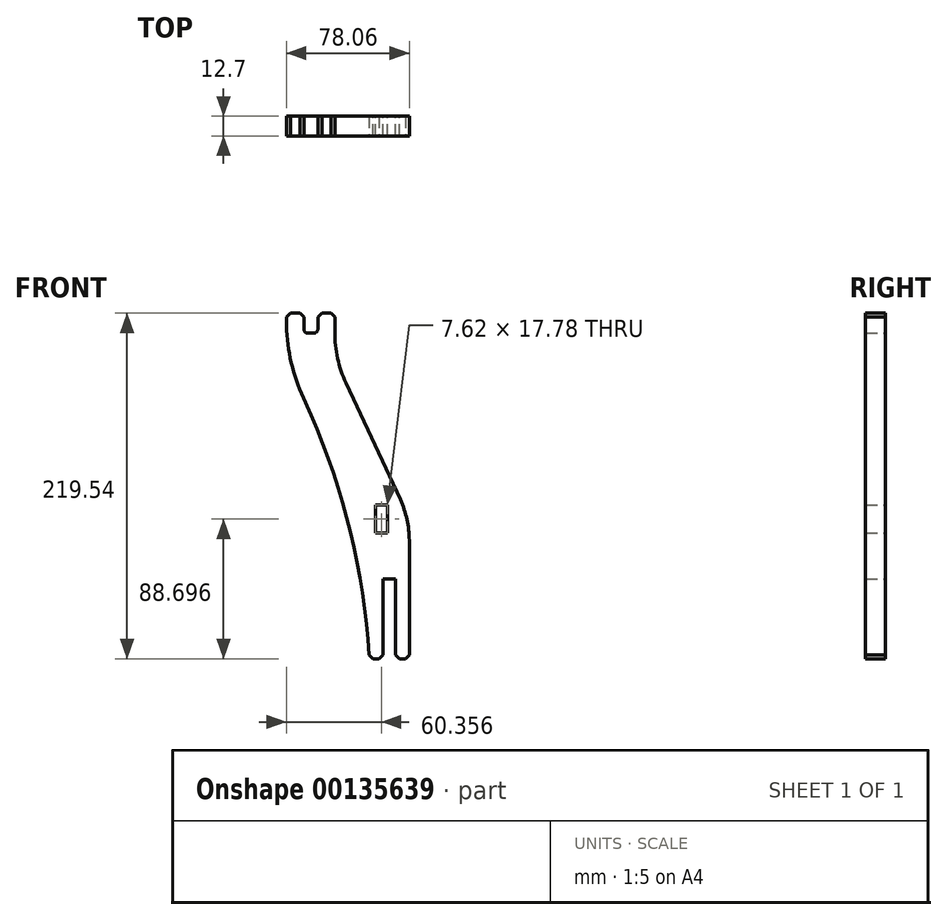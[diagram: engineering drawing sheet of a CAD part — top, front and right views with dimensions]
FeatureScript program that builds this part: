
annotation { "Feature Type Name" : "Feature", "Feature Type Description" : "" }
export const myFeature = defineFeature(function(context is Context, id is Id, definition is map)
    precondition{}
    {
        {
            var Q0;
            Q0=qCreatedBy(makeId("Front.planeOp"),FACE);
            var sketch = newSketch(context, id + "F0", { "sketchPlane" : qUnion([Q0])});
            skLineSegment(sketch, "E0.bottom", {"start": v(9.01, 35.53) * mm, "end": v(34.67, 35.53) * mm});
            skLineSegment(sketch, "E0.top", {"start": v(9.01, -35.53) * mm, "end": v(34.67, -35.53) * mm});
            skLineSegment(sketch, "E0.left", {"start": v(9.01, 35.53) * mm, "end": v(9.01, -35.53) * mm});
            skLineSegment(sketch, "E0.right", {"start": v(34.67, 35.53) * mm, "end": v(34.67, -35.53) * mm});
            skPoint(sketch, "E0.middle", {"position": v(21.84, 0) * mm});
            skLineSegment(sketch, "E1.bottom", {"start": v(17.9, -35.53) * mm, "end": v(25.78, -35.53) * mm});
            skLineSegment(sketch, "E1.top", {"start": v(17.9, 15.27) * mm, "end": v(25.78, 15.27) * mm});
            skLineSegment(sketch, "E1.left", {"start": v(17.9, -35.53) * mm, "end": v(17.9, 15.27) * mm});
            skLineSegment(sketch, "E1.right", {"start": v(25.78, -35.53) * mm, "end": v(25.78, 15.27) * mm});
            skLineSegment(sketch, "E2", {"start": v(34.67, 35.53) * mm, "end": v(34.67, 53.31) * mm});
            skLineSegment(sketch, "E3.bottom", {"start": v(-12.63, 154.91) * mm, "end": v(-43.39, 154.91) * mm});
            skLineSegment(sketch, "E3.top", {"start": v(-12.63, 184.01) * mm, "end": v(-43.39, 184.01) * mm});
            skLineSegment(sketch, "E3.left", {"start": v(-12.63, 154.91) * mm, "end": v(-12.63, 184.01) * mm});
            skLineSegment(sketch, "E3.right", {"start": v(-43.39, 154.91) * mm, "end": v(-43.39, 184.01) * mm});
            skPoint(sketch, "E3.middle", {"position": v(-28, 169.46) * mm});
            skLineSegment(sketch, "E4.bottom", {"start": v(-32.33, 184.01) * mm, "end": v(-23.44, 184.01) * mm});
            skLineSegment(sketch, "E4.top", {"start": v(-29.79, 171.31) * mm, "end": v(-25.98, 171.31) * mm});
            skLineSegment(sketch, "E4.left", {"start": v(-32.33, 184.01) * mm, "end": v(-32.33, 173.85) * mm});
            skLineSegment(sketch, "E4.right", {"start": v(-23.44, 184.01) * mm, "end": v(-23.44, 173.85) * mm});
            skLineSegment(sketch, "E5", {"start": v(-12.63, 154.91) * mm, "end": v(34.67, 53.31) * mm});
            skLineSegment(sketch, "E6", {"start": v(-43.39, 154.91) * mm, "end": v(9.01, 35.53) * mm});
            skPoint(sketch, "E7.visualSharp", {"position": v(-32.33, 171.31) * mm});
            skArc(sketch, "E7.filletArc", {"start": v(-32.33, 173.85) * mm, "mid": v(-31.58, 172.06) * mm, "end": v(-29.79, 171.31) * mm});
            skPoint(sketch, "E8.visualSharp", {"position": v(-23.44, 171.31) * mm});
            skArc(sketch, "E8.filletArc", {"start": v(-25.98, 171.31) * mm, "mid": v(-24.18, 172.06) * mm, "end": v(-23.44, 173.85) * mm});
            skLineSegment(sketch, "E9.bottom", {"start": v(13.16, 62.06) * mm, "end": v(20.78, 62.06) * mm});
            skLineSegment(sketch, "E9.top", {"start": v(13.16, 44.28) * mm, "end": v(20.78, 44.28) * mm});
            skLineSegment(sketch, "E9.left", {"start": v(13.16, 62.06) * mm, "end": v(13.16, 44.28) * mm});
            skLineSegment(sketch, "E9.right", {"start": v(20.78, 62.06) * mm, "end": v(20.78, 44.28) * mm});
            skSolve(sketch);
        }
        {
            var Q0;
            Q0=makeQuery(id+"F0.imprint","IMPRINT",FACE,{"disambiguationData":[TD([[makeQuery(id+"F0.imprint","IMPRINT",EDGE,{"derivedFrom":sQuery(id+"F0.wireOp",EDGE,"E3.bottom")}),-1.0]])]});
            var Q1;
            Q1=makeQuery(id+"F0.imprint","IMPRINT",FACE,{"disambiguationData":[TD([[makeQuery(id+"F0.imprint","IMPRINT",EDGE,{"derivedFrom":sQuery(id+"F0.wireOp",EDGE,"E0.bottom")}),1.0]])]});
            var Q2;
            Q2=makeQuery(id+"F0.imprint","IMPRINT",FACE,{"disambiguationData":[TD([[makeQuery(id+"F0.imprint","IMPRINT",EDGE,{"derivedFrom":sQuery(id+"F0.wireOp",EDGE,"E0.bottom")}),-1.0]])]});
            extrude(context, id + "F1", {"entities" : qUnion([Q0, Q1, Q2]), "depth" : 12.7 * mm});
        }
        {
            var Q0;
            Q0=makeQuery(id+"F1.opExtrude","SWEPT_EDGE",EDGE,{"disambiguationData":[OSD([sQuery(id+"F0.wireOp",EDGE,"E3.top"),sQuery(id+"F0.wireOp",EDGE,"E4.bottom"),sQuery(id+"F0.wireOp",EDGE,"E4.left")])]});
            var Q1;
            Q1=makeQuery(id+"F1.opExtrude","SWEPT_EDGE",EDGE,{"disambiguationData":[OSD([sQuery(id+"F0.wireOp",EDGE,"E3.top"),sQuery(id+"F0.wireOp",EDGE,"E4.bottom"),sQuery(id+"F0.wireOp",EDGE,"E4.right")])]});
            var Q2;
            Q2=makeQuery(id+"F1.opExtrude","SWEPT_EDGE",EDGE,{"disambiguationData":[OSD([sQuery(id+"F0.wireOp",EDGE,"E3.top"),sQuery(id+"F0.wireOp",EDGE,"E3.left")])]});
            var Q3;
            Q3=makeQuery(id+"F1.opExtrude","SWEPT_EDGE",EDGE,{"disambiguationData":[OSD([sQuery(id+"F0.wireOp",EDGE,"E3.top"),sQuery(id+"F0.wireOp",EDGE,"E3.right")])]});
            var Q4;
            Q4=makeQuery(id+"F1.opExtrude","SWEPT_EDGE",EDGE,{"disambiguationData":[OSD([sQuery(id+"F0.wireOp",EDGE,"E0.top"),sQuery(id+"F0.wireOp",EDGE,"E1.bottom"),sQuery(id+"F0.wireOp",EDGE,"E1.left")])]});
            var Q5;
            Q5=makeQuery(id+"F1.opExtrude","SWEPT_EDGE",EDGE,{"disambiguationData":[OSD([sQuery(id+"F0.wireOp",EDGE,"E0.top"),sQuery(id+"F0.wireOp",EDGE,"E1.bottom"),sQuery(id+"F0.wireOp",EDGE,"E1.right")])]});
            var Q6;
            Q6=makeQuery(id+"F1.opExtrude","SWEPT_EDGE",EDGE,{"disambiguationData":[OSD([sQuery(id+"F0.wireOp",EDGE,"E0.top"),sQuery(id+"F0.wireOp",EDGE,"E0.right")])]});
            var Q7;
            Q7=makeQuery(id+"F1.opExtrude","SWEPT_EDGE",EDGE,{"disambiguationData":[OSD([sQuery(id+"F0.wireOp",EDGE,"E0.top"),sQuery(id+"F0.wireOp",EDGE,"E0.left")])]});
            chamfer(context, id + "F2", {"entities" : qUnion([Q0, Q1, Q2, Q3, Q4, Q5, Q6, Q7]), "width" : 2.54 * mm, "tangentPropagation" : true});
        }
        {
            var Q0;
            Q0=makeQuery(id+"F1.opExtrude","SWEPT_EDGE",EDGE,{"disambiguationData":[OSD([sQuery(id+"F0.wireOp",EDGE,"E2"),sQuery(id+"F0.wireOp",EDGE,"E5")])]});
            fillet(context, id + "F3", {"entities" : qUnion([Q0]), "radius" : 61.32 * mm, "tangentPropagation" : true, "allowEdgeOverflow" : false});
        }
        {
            var Q0;
            Q0=makeQuery(id+"F1.opExtrude","SWEPT_EDGE",EDGE,{"disambiguationData":[OSD([sQuery(id+"F0.wireOp",EDGE,"E3.bottom"),sQuery(id+"F0.wireOp",EDGE,"E3.left"),sQuery(id+"F0.wireOp",EDGE,"E5")])]});
            fillet(context, id + "F4", {"entities" : qUnion([Q0]), "radius" : 76.32 * mm, "tangentPropagation" : true, "allowEdgeOverflow" : false});
        }
        {
            var Q0;
            Q0=makeQuery(id+"F1.opExtrude","SWEPT_EDGE",EDGE,{"disambiguationData":[OSD([sQuery(id+"F0.wireOp",EDGE,"E3.bottom"),sQuery(id+"F0.wireOp",EDGE,"E3.right"),sQuery(id+"F0.wireOp",EDGE,"E6")])]});
            fillet(context, id + "F5", {"entities" : qUnion([Q0]), "radius" : 114.03 * mm, "tangentPropagation" : true, "allowEdgeOverflow" : false});
        }
        {
            var Q0;
            Q0=makeQuery(id+"F1.opExtrude","SWEPT_EDGE",EDGE,{"disambiguationData":[OSD([sQuery(id+"F0.wireOp",EDGE,"E0.bottom"),sQuery(id+"F0.wireOp",EDGE,"E0.left"),sQuery(id+"F0.wireOp",EDGE,"E6")])]});
            fillet(context, id + "F6", {"entities" : qUnion([Q0]), "radius" : 446.18 * mm, "tangentPropagation" : true, "allowEdgeOverflow" : false});
        }
    });
